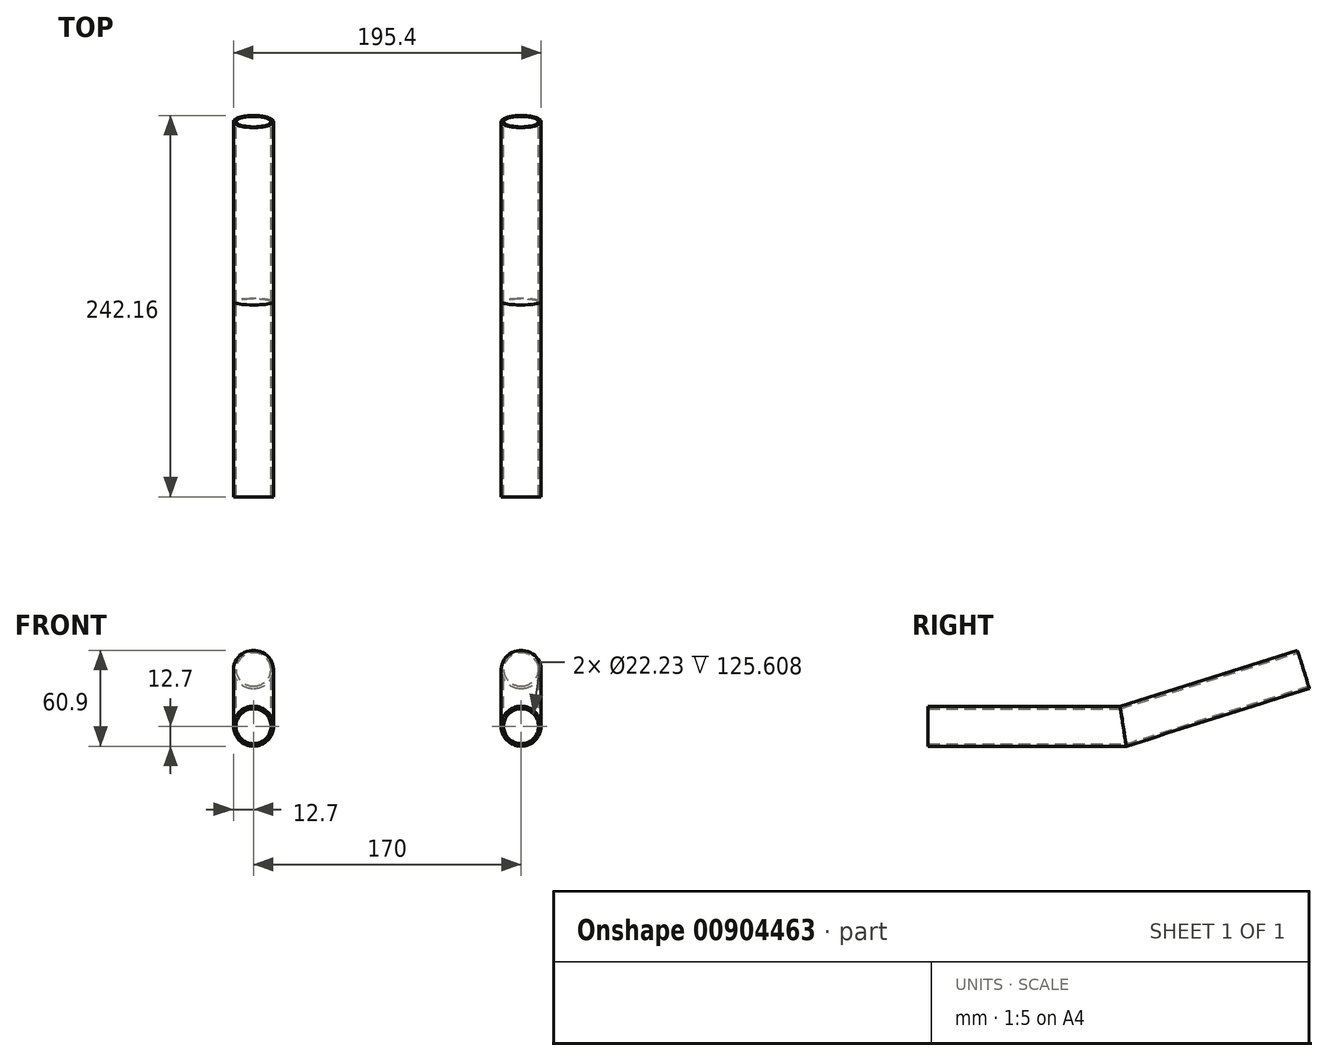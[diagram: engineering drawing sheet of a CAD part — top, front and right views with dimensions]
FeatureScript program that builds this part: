
annotation { "Feature Type Name" : "Feature", "Feature Type Description" : "" }
export const myFeature = defineFeature(function(context is Context, id is Id, definition is map)
    precondition{}
    {
        {
            var Q0;
            Q0=qCreatedBy(makeId("Top.planeOp"),FACE);
            var sketch = newSketch(context, id + "F0", { "sketchPlane" : qUnion([Q0])});
            skLineSegment(sketch, "E0", {"start": v(-85, 49.74) * mm, "end": v(-85, -74.15) * mm});
            skLineSegment(sketch, "E1", {"start": v(85, 49.74) * mm, "end": v(85, -74.15) * mm});
            skLineSegment(sketch, "E2", {"start": v(-85, 49.74) * mm, "end": v(85, 49.74) * mm, "construction": true});
            skSolve(sketch);
        }
        {
            var Q0;
            Q0=sQuery(id+"F0.wireOp",EDGE,"E2");
            cPlane(context, id + "F1", {"entities" : qUnion([Q0]), "cplaneType" : CPlaneType.LINE_ANGLE, "offset" : 25 * mm, "angle" : 72.5 * degree, "oppositeDirection" : true, "width" : 150 * mm, "height" : 150 * mm});
        }
        {
            var Q0;
            Q0=qCreatedBy(id+"F1.planeOp",FACE);
            var sketch = newSketch(context, id + "F2", { "sketchPlane" : qUnion([Q0])});
            skLineSegment(sketch, "E3", {"start": v(85, -47.44) * mm, "end": v(85, -167.44) * mm});
            skLineSegment(sketch, "E4", {"start": v(-85, -47.44) * mm, "end": v(-85, -167.44) * mm});
            skLineSegment(sketch, "E5", {"start": v(-85, -167.44) * mm, "end": v(85, -167.44) * mm, "construction": true});
            skLineSegment(sketch, "E6", {"start": v(-77.97, -252.44) * mm, "end": v(126.28, -252.44) * mm, "construction": true});
            skPoint(sketch, "E6.startSnap0", {"position": v(0, -252.44) * mm});
            skSolve(sketch);
        }
        {
            var Q0;
            Q0=qCreatedBy(makeId("Front.planeOp"),FACE);
            var Q1;
            Q1=sQuery(id+"F0.wireOp",VERTEX,"E0.end");
            cPlane(context, id + "F3", {"entities" : qUnion([Q0, Q1]), "cplaneType" : CPlaneType.PLANE_POINT, "offset" : 25 * mm, "width" : 150 * mm, "height" : 150 * mm});
        }
        {
            var Q0;
            Q0=qCreatedBy(id+"F3.planeOp",FACE);
            var sketch = newSketch(context, id + "F4", { "sketchPlane" : qUnion([Q0])});
            skCircle(sketch, "E7", {"center": v(-85, 0) * mm, "radius": 12.7 * mm});
            skCircle(sketch, "E8", {"center": v(-85, 0) * mm, "radius": 11.11 * mm});
            skSolve(sketch);
        }
        {
            var Q0;
            Q0=qSketchRegion(id+"F4",true);
            var Q1;
            Q1=sQuery(id+"F0.wireOp",EDGE,"E0");
            var Q2;
            Q2=sQuery(id+"F2.wireOp",EDGE,"E4");
            sweep(context, id + "F5", {"profiles" : qUnion([Q0]), "path" : qUnion([Q1, Q2])});
        }
        {
            var Q0;
            Q0=qCreatedBy(id+"F3.planeOp",FACE);
            var sketch = newSketch(context, id + "F6", { "sketchPlane" : qUnion([Q0])});
            skCircle(sketch, "E9", {"center": v(85, 0) * mm, "radius": 12.7 * mm});
            skCircle(sketch, "E10", {"center": v(85, 0) * mm, "radius": 11.11 * mm});
            skSolve(sketch);
        }
        {
            var Q0;
            Q0 = qSketchRegion(id + "F6", true);
            var Q1;
            Q1=sQuery(id+"F0.wireOp",EDGE,"E1");
            var Q2;
            Q2=sQuery(id+"F2.wireOp",EDGE,"E3");
            sweep(context, id + "F7", {"profiles" : qUnion([Q0]), "path" : qUnion([Q1, Q2])});
        }
    });
